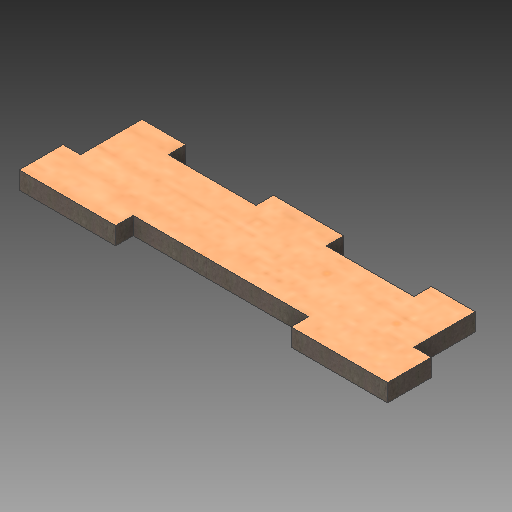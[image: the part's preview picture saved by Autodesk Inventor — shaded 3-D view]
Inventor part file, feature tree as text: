
AUTODESK INVENTOR PART (.ipt)
format: ipt  version: 2019 (Build 230136000, 136)  size: 159,744 bytes
history: native  units: mm
features: other x1, extrude x1, sketch x1
ambient origin geometry x8: Origin, YZ Plane, XZ Plane, XY Plane, X Axis, Y Axis, Z Axis, Center Point
bodies: Body1 (feature_tree)
feature tree (3):
  other  "Твердое тело1"
  extrude  "Выдавливание1"  Depth=10.0mm
  sketch  "Эскиз1"
